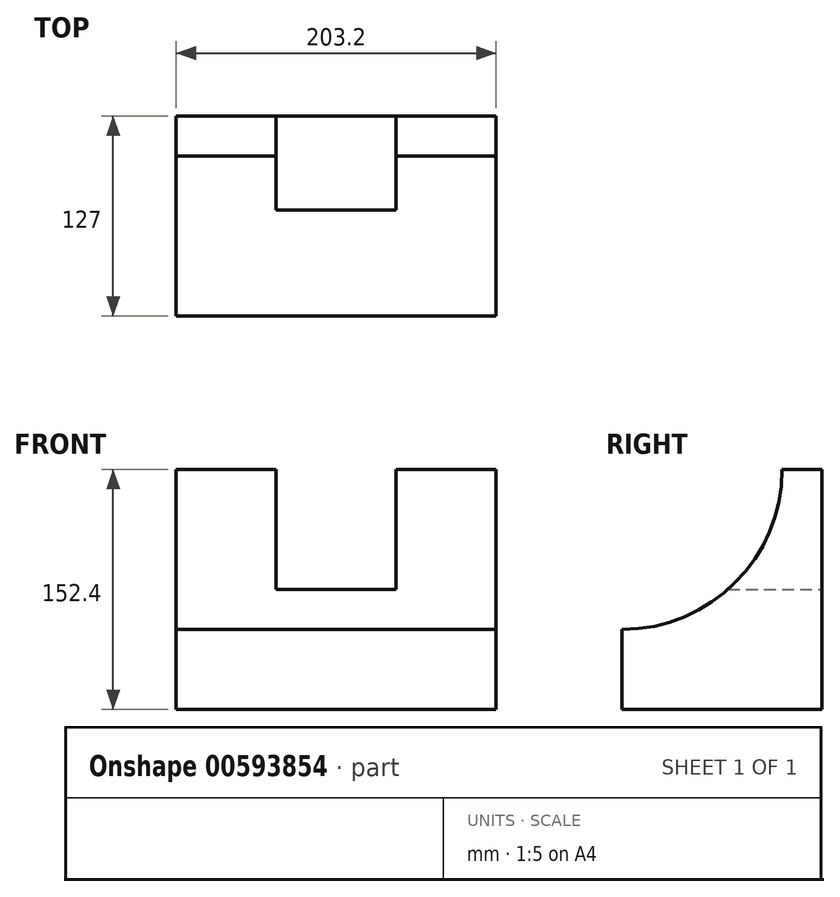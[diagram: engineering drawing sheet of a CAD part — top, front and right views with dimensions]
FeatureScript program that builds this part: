
annotation { "Feature Type Name" : "Feature", "Feature Type Description" : "" }
export const myFeature = defineFeature(function(context is Context, id is Id, definition is map)
    precondition{}
    {
        {
            var Q0;
            Q0=qCreatedBy(makeId("Right.planeOp"),FACE);
            var sketch = newSketch(context, id + "F0", { "sketchPlane" : qUnion([Q0])});
            skLineSegment(sketch, "E0.bottom", {"start": v(0, 0) * mm, "end": v(-127, 0) * mm});
            skLineSegment(sketch, "E0.top", {"start": v(0, 152.4) * mm, "end": v(-127, 152.4) * mm});
            skLineSegment(sketch, "E0.left", {"start": v(0, 0) * mm, "end": v(0, 152.4) * mm});
            skLineSegment(sketch, "E0.right", {"start": v(-127, 0) * mm, "end": v(-127, 152.4) * mm});
            skArc(sketch, "E1", {"start": v(-127, 50.8) * mm, "mid": v(-55.16, 80.56) * mm, "end": v(-25.4, 152.4) * mm});
            skSolve(sketch);
        }
        {
            var Q0;
            {var subQ1=sQuery(id+"F0.wireOp",EDGE,"E0.bottom");Q0=makeQuery(id+"F0.imprint","IMPRINT",FACE,{"disambiguationData":[TD([[makeQuery(id+"F0.imprint","IMPRINT",EDGE,{"derivedFrom":subQ1}),-1.0]])]});}
            extrude(context, id + "F1", {"entities" : qUnion([Q0]), "endBound" : BoundingType.SYMMETRIC, "depth" : 203.2 * mm, "offsetDistance" : 25.4 * mm});
        }
        {
            var Q0;
            Q0=makeQuery(id+"F1.opExtrude","SWEPT_FACE",FACE,{"disambiguationData":[OSD([sQuery(id+"F0.wireOp",EDGE,"E0.left")])]});
            var sketch = newSketch(context, id + "F2", { "sketchPlane" : qUnion([Q0])});
            skLineSegment(sketch, "E2.bottom", {"start": v(-38.1, 152.4) * mm, "end": v(38.1, 152.4) * mm});
            skLineSegment(sketch, "E2.top", {"start": v(-38.1, 76.2) * mm, "end": v(38.1, 76.2) * mm});
            skLineSegment(sketch, "E2.left", {"start": v(-38.1, 152.4) * mm, "end": v(-38.1, 76.2) * mm});
            skLineSegment(sketch, "E2.right", {"start": v(38.1, 152.4) * mm, "end": v(38.1, 76.2) * mm});
            skPoint(sketch, "E3", {"position": v(0, 152.4) * mm});
            skSolve(sketch);
        }
        {
            var Q0;
            Q0=makeQuery(id+"F2.imprint","IMPRINT",FACE,{"disambiguationData":[TD([[makeQuery(id+"F2.imprint","IMPRINT",EDGE,{"derivedFrom":sQuery(id+"F2.wireOp",EDGE,"E2.bottom")}),-1.0]])]});
            var Q1;
            Q1=makeQuery(id+"F1.opExtrude","SWEPT_FACE",FACE,{"disambiguationData":[OSD([sQuery(id+"F0.wireOp",EDGE,"E1")])]});
            extrude(context, id + "F3", {"entities" : qUnion([Q0]), "operationType" : NewBodyOperationType.REMOVE, "endBound" : BoundingType.UP_TO_SURFACE, "oppositeDirection" : true, "depth" : 25.4 * mm, "endBoundEntityFace" : qUnion([Q1]), "offsetDistance" : 25.4 * mm});
        }
    });
